# Revit family: ISI_IdealStandard_WCSeats_Concept_E8225
name_source: partatom
category: Plumbing Fixtures
revit_build: Autodesk Revit MEP 2012 (Build: 20110309_2315(x64)
units: mm (PartAtom-declared; Revit-internal decimal feet)

## types (1)
- E822501-Concept Freedom seat and cover for elongated pan
    Accessories = www.idealspec.co.uk
    AreaUnits = millimeters
    Assembly Code = C1030200
    AssetType = Fixed
    BIMObjectName = ISI_IdealStandard_WCSeats_ConceptFreedom-Seat&Cover-ElongatedPan_E8225
    Brand = Ideal Standard
    CWFU = 0
    Color = White
    ConnectionType = Plumbing
    Cost = 0 $
    Default Elevation = 1219 mm
    Description = Concept freedom seat and cover for elongated pan
    DurationUnit = year
    ECA = No
    ExpectedLife = 15
    Features = Seat and cover for elongated pan
    Finish = White
    HWFU = 0
    Help = www.idealspec.co.uk/contact-us.html
    IfcExportAs = IfcSanitaryTerminalType
    IfcExportType = WCSEAT
    InstallationInstructions = www.idealspec.co.uk/resources.html
    LinearUnits = millimeters
    ManufacturerURL = www.idealspec.co.uk
    Material = Plastic
    Model = E822501
    ModelNumber = E822501
    ModelReference = Concept freedom seat and cover for elongated pan
    NBSDescription = WC seats and covers
    NBSReference = 45-35-70/391
    Name = WCSeats_ConceptFreedom-Seat&Cover-ElongatedPan-E8225_IdealStandard
    NettWeight = 1.4 Kg
    NominalDepth = 435 mm
    NominalHeight = 45 mm
    NominalLength = 435 mm
    NominalWidth = 366 mm
    ProductInformation = www.idealspec.co.uk/assets/datasheet/E822501
    SeatColor = White
    SeatHasCover = Yes
    SeatMaterial = Plastic
    SeatSKU = Plastic
    SeatType = RingSeat
    Shape = Ring
    Size = 366 x 435 x 45 mm
    Space = Internal
    SpareParts = www.fastpart-spares.co.uk
    URL = www.idealspec.co.uk
    Uniclass2 = Pr_40_20_93_95
    Version = 2
    VolumeUnits = Litres
    WFU = 0
    WRAS = No
    WarrantyDescription = Manufacturers Warranty
    WarrantyDurationParts = 5
    WarrantyDurationUnit = year
    WaterEfficientProduct = No

## geometry (parser evidence)
native form markers: Sweep x5
no freeform markers — native parametric forms only
